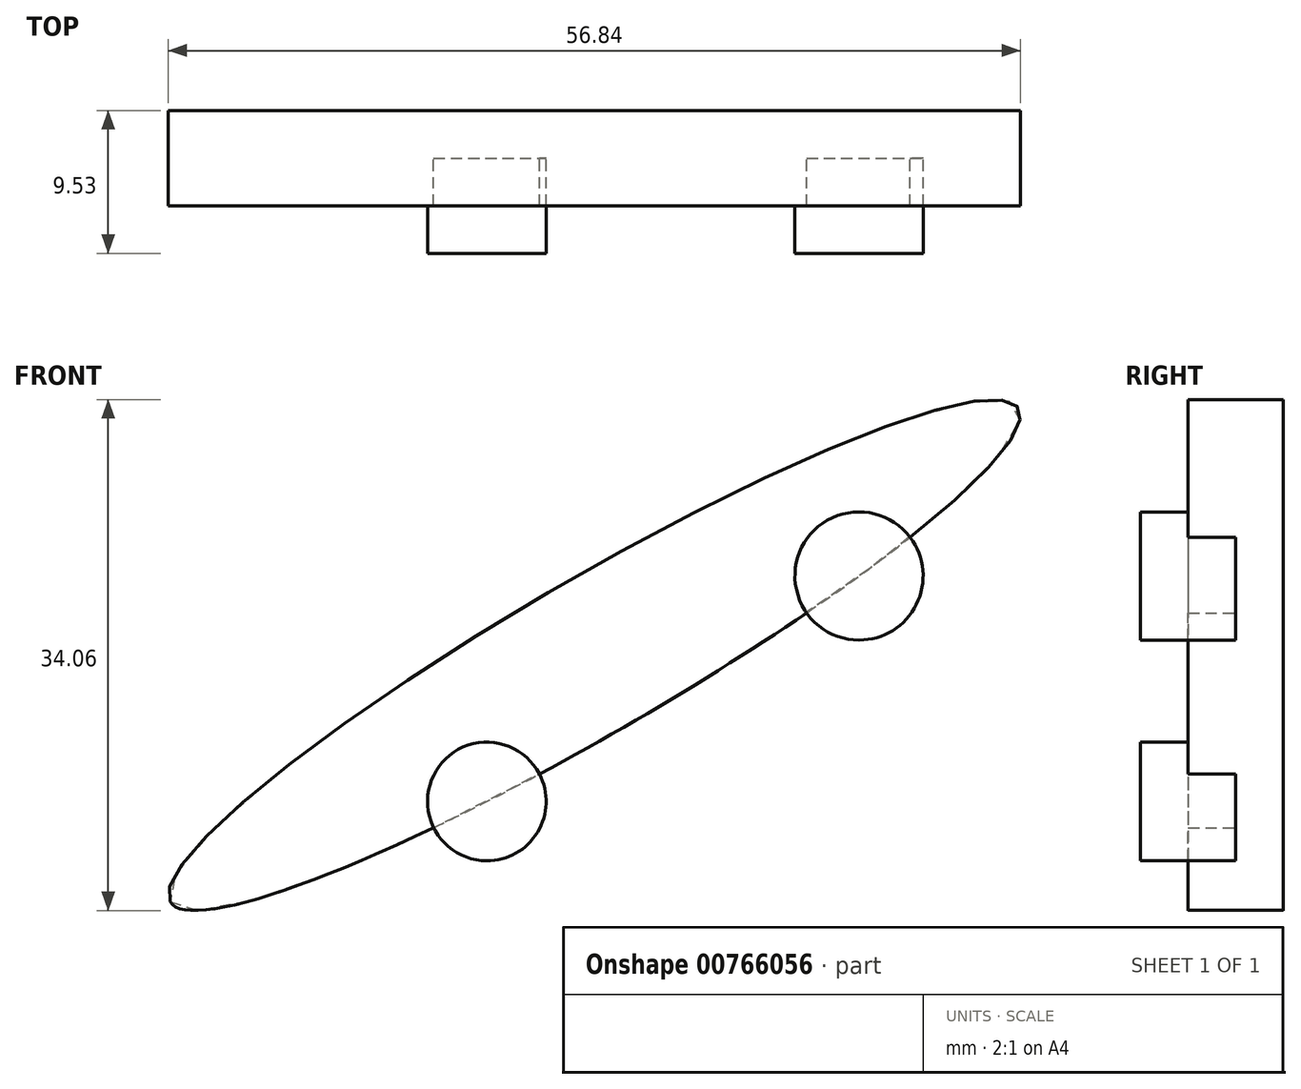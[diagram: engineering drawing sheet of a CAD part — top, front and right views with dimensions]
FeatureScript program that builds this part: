
annotation { "Feature Type Name" : "Feature", "Feature Type Description" : "" }
export const myFeature = defineFeature(function(context is Context, id is Id, definition is map)
    precondition{}
    {
        {
            var Q0;
            Q0=qCreatedBy(makeId("Front.planeOp"),FACE);
            var sketch = newSketch(context, id + "F0", { "sketchPlane" : qUnion([Q0])});
            skEllipse(sketch, "E0", {"center": v(19.24, 15.57) * mm, "majorRadius": 32.73 * mm, "minorRadius": 5.15 * mm, "majorAxis": v(-0.86, -0.5)});
            skSolve(sketch);
        }
        {
            var Q0;
            Q0=qCreatedBy(makeId("Front.planeOp"),FACE);
            var sketch = newSketch(context, id + "F1", { "sketchPlane" : qUnion([Q0])});
            skCircle(sketch, "E1", {"center": v(10.65, 4.19) * mm, "radius": 3.68 * mm});
            skCircle(sketch, "E2", {"center": v(35.14, 18.9) * mm, "radius": 3.97 * mm});
            skSolve(sketch);
        }
        {
            var Q0;
            Q0=makeQuery(id+"F0.imprint","IMPRINT",FACE,{"disambiguationData":[TD([[makeQuery(id+"F0.imprint","IMPRINT",EDGE,{"derivedFrom":sQuery(id+"F0.wireOp",EDGE,"E0")}),1.0]])]});
            extrude(context, id + "F2", {"entities" : qUnion([Q0]), "depth" : 6.35 * mm, "offsetDistance" : 25.4 * mm});
        }
        {
            var Q0;
            Q0=sQuery(id+"F1.wireOp",EDGE,"E1");
            var Q1;
            Q1=sQuery(id+"F1.wireOp",EDGE,"E2");
            extrude(context, id + "F3", {"bodyType" : ToolBodyType.SURFACE, "surfaceEntities" : qUnion([Q0, Q1]), "endBound" : BoundingType.SYMMETRIC, "depth" : 6.35 * mm, "offsetDistance" : 25.4 * mm});
        }
        {
            var Q0;
            Q0=makeQuery(id+"F2.opExtrude","CAP_FACE",FACE,{"disambiguationData":[OSD([sQuery(id+"F0.wireOp",EDGE,"E0")])],"isStart":false});
            var sketch = newSketch(context, id + "F4", { "sketchPlane" : qUnion([Q0])});
            skCircle(sketch, "E3", {"center": v(12.07, 5.8) * mm, "radius": 3.95 * mm});
            skCircle(sketch, "E4", {"center": v(36.89, 20.84) * mm, "radius": 4.27 * mm});
            skSolve(sketch);
        }
        {
            var Q0;
            Q0 = qSketchRegion(id + "F4", true);
            extrude(context, id + "F5", {"entities" : qUnion([Q0]), "operationType" : NewBodyOperationType.ADD, "endBound" : BoundingType.SYMMETRIC, "depth" : 6.35 * mm, "offsetDistance" : 25.4 * mm});
        }
    });
